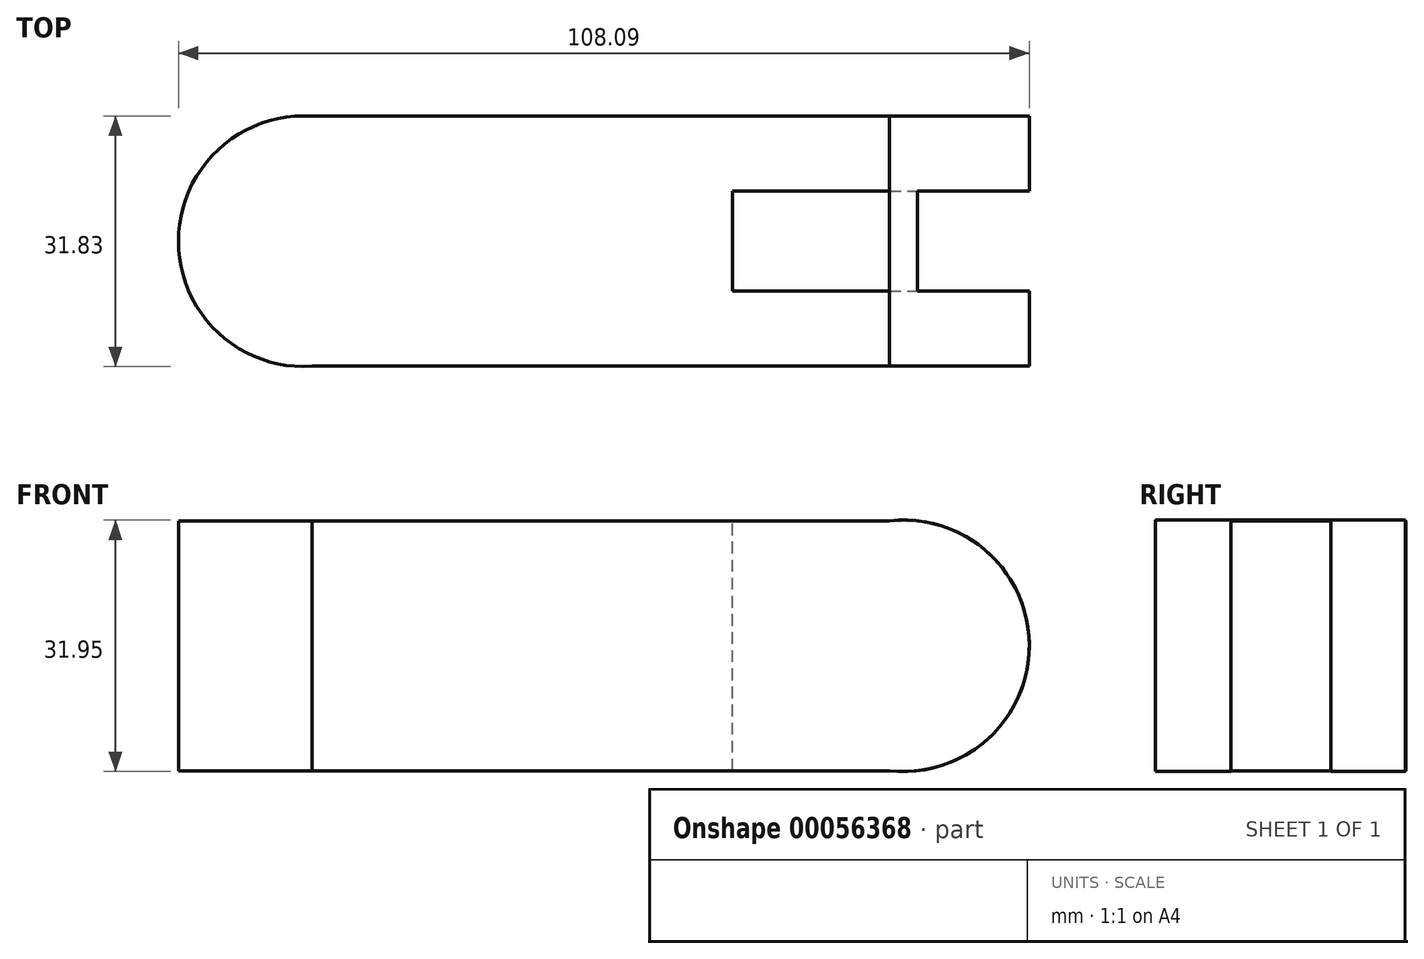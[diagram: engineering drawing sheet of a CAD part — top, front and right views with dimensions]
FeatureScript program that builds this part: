
annotation { "Feature Type Name" : "Feature", "Feature Type Description" : "" }
export const myFeature = defineFeature(function(context is Context, id is Id, definition is map)
    precondition{}
    {
        {
            var Q0;
            Q0=qCreatedBy(makeId("Front.planeOp"),FACE);
            var sketch = newSketch(context, id + "F0", { "sketchPlane" : qUnion([Q0])});
            skLineSegment(sketch, "E0.bottom", {"start": v(-31.79, 18.5) * mm, "end": v(44.41, 18.5) * mm});
            skLineSegment(sketch, "E0.top", {"start": v(-31.79, -13.25) * mm, "end": v(44.41, -13.25) * mm});
            skLineSegment(sketch, "E0.left", {"start": v(-31.79, 18.5) * mm, "end": v(-31.79, -13.25) * mm});
            skLineSegment(sketch, "E0.right", {"start": v(44.41, 18.5) * mm, "end": v(44.41, -13.25) * mm});
            skSolve(sketch);
        }
        {
            var Q0;
            Q0 = qSketchRegion(id + "F0", true);
            extrude(context, id + "F1", {"entities" : qUnion([Q0]), "depth" : 31.75 * mm});
        }
        {
            var Q0;
            Q0=makeQuery(id+"F1.opExtrude","CAP_FACE",FACE,{"disambiguationData":[OSD([sQuery(id+"F0.wireOp",EDGE,"E0.bottom"),sQuery(id+"F0.wireOp",EDGE,"E0.top"),sQuery(id+"F0.wireOp",EDGE,"E0.left"),sQuery(id+"F0.wireOp",EDGE,"E0.right")])],"isStart":false});
            var sketch = newSketch(context, id + "F2", { "sketchPlane" : qUnion([Q0])});
            skCircle(sketch, "E1", {"center": v(44.41, 2.63) * mm, "radius": 15.98 * mm});
            skSolve(sketch);
        }
        {
            var Q0;
            Q0 = qSketchRegion(id + "F2", true);
            extrude(context, id + "F3", {"entities" : qUnion([Q0]), "operationType" : NewBodyOperationType.ADD, "oppositeDirection" : true, "depth" : 31.75 * mm});
        }
        {
            var Q0;
            Q0=makeQuery(id+"F1.opExtrude","SWEPT_FACE",FACE,{"disambiguationData":[OSD([sQuery(id+"F0.wireOp",EDGE,"E0.bottom")])]});
            var sketch = newSketch(context, id + "F4", { "sketchPlane" : qUnion([Q0])});
            skCircle(sketch, "E2", {"center": v(-31.79, -15.88) * mm, "radius": 15.91 * mm});
            skSolve(sketch);
        }
        {
            var Q0;
            Q0 = qSketchRegion(id + "F4", true);
            extrude(context, id + "F5", {"entities" : qUnion([Q0]), "operationType" : NewBodyOperationType.ADD, "oppositeDirection" : true, "depth" : 31.75 * mm});
        }
        {
            var Q0;
            Q0=makeQuery(id+"F5.boolean.opBoolean","MERGE",FACE,{"derivedFrom":[makeQuery(id+"F1.opExtrude","SWEPT_FACE",FACE,{"disambiguationData":[OSD([sQuery(id+"F0.wireOp",EDGE,"E0.bottom")])]}),makeQuery(id+"F5.opExtrude","CAP_FACE",FACE,{"disambiguationData":[OSD([sQuery(id+"F4.wireOp",EDGE,"E2")])],"isStart":true})]});
            var sketch = newSketch(context, id + "F6", { "sketchPlane" : qUnion([Q0])});
            skLineSegment(sketch, "E3.bottom", {"start": v(22.67, -9.47) * mm, "end": v(60.77, -9.47) * mm});
            skLineSegment(sketch, "E3.top", {"start": v(22.67, -22.17) * mm, "end": v(60.77, -22.17) * mm});
            skLineSegment(sketch, "E3.left", {"start": v(22.67, -9.47) * mm, "end": v(22.67, -22.17) * mm});
            skLineSegment(sketch, "E3.right", {"start": v(60.77, -9.47) * mm, "end": v(60.77, -22.17) * mm});
            skSolve(sketch);
        }
        {
            var Q0;
            Q0 = qSketchRegion(id + "F6", true);
            extrude(context, id + "F7", {"entities" : qUnion([Q0]), "operationType" : NewBodyOperationType.REMOVE, "endBound" : BoundingType.THROUGH_ALL, "oppositeDirection" : true, "depth" : 25.4 * mm});
        }
    });
